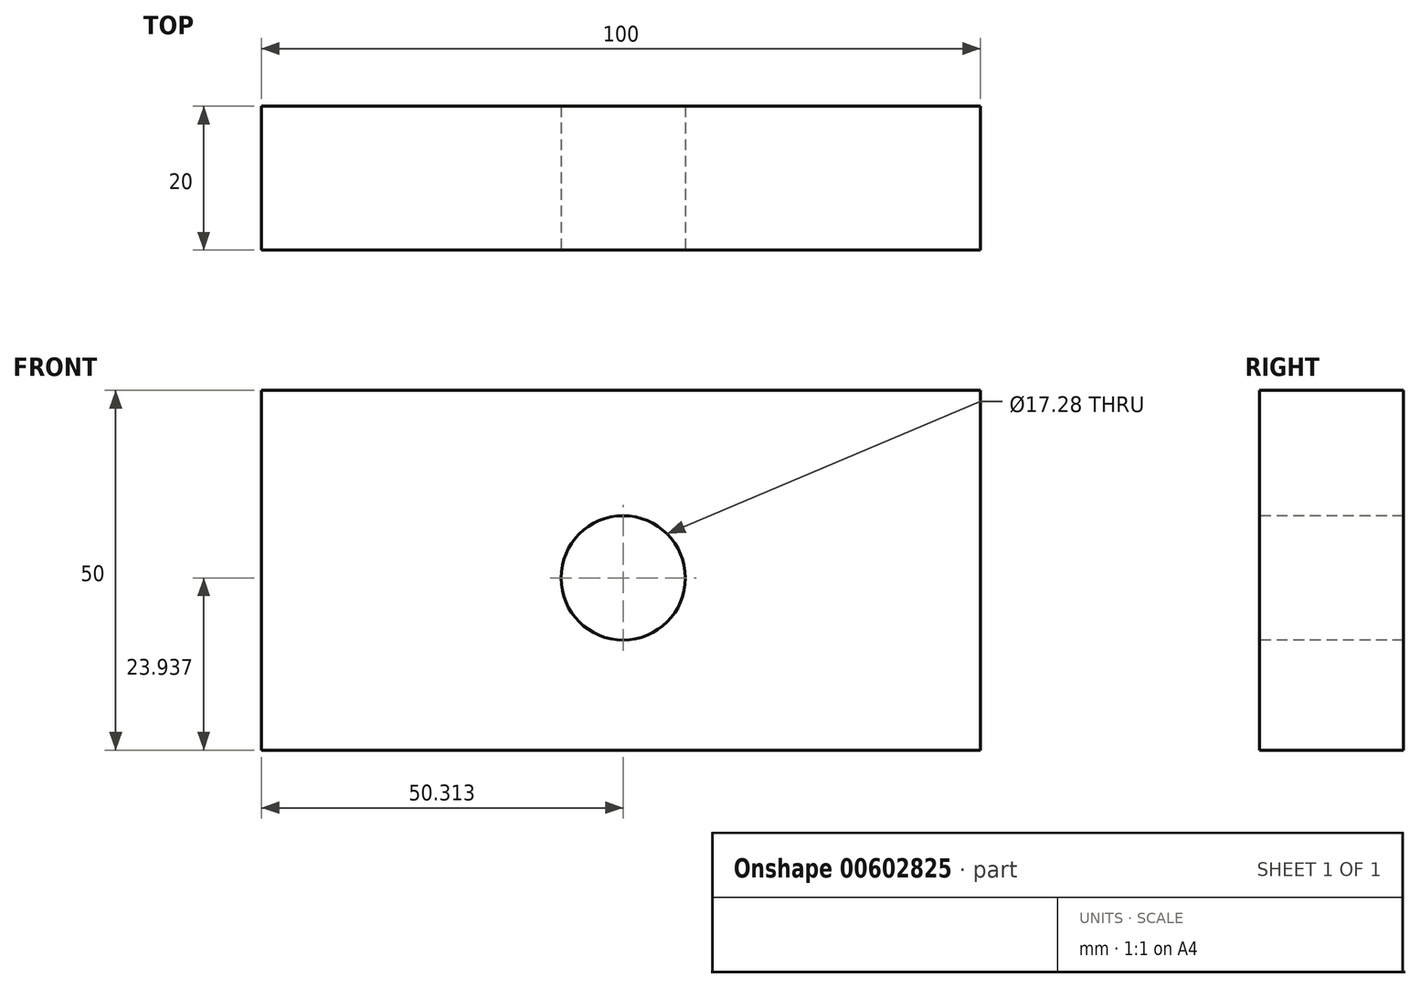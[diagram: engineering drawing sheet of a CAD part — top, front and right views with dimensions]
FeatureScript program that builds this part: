
annotation { "Feature Type Name" : "Feature", "Feature Type Description" : "" }
export const myFeature = defineFeature(function(context is Context, id is Id, definition is map)
    precondition{}
    {
        {
            var Q0;
            Q0=qCreatedBy(makeId("Front.planeOp"),FACE);
            var sketch = newSketch(context, id + "F0", { "sketchPlane" : qUnion([Q0])});
            skLineSegment(sketch, "E0.bottom", {"start": v(0, 0) * mm, "end": v(100, 0) * mm});
            skLineSegment(sketch, "E0.top", {"start": v(0, 50) * mm, "end": v(100, 50) * mm});
            skLineSegment(sketch, "E0.left", {"start": v(0, 0) * mm, "end": v(0, 50) * mm});
            skLineSegment(sketch, "E0.right", {"start": v(100, 0) * mm, "end": v(100, 50) * mm});
            skSolve(sketch);
        }
        {
            var Q0;
            Q0=makeQuery(id+"F0.imprint","IMPRINT",FACE,{"disambiguationData":[TD([[makeQuery(id+"F0.imprint","IMPRINT",EDGE,{"derivedFrom":sQuery(id+"F0.wireOp",EDGE,"E0.bottom")}),1.0]])]});
            extrude(context, id + "F1", {"entities" : qUnion([Q0]), "depth" : 20 * mm, "offsetDistance" : 25 * mm});
        }
        {
            var Q0;
            Q0=makeQuery(id+"F1.opExtrude","CAP_FACE",FACE,{"disambiguationData":[OSD([sQuery(id+"F0.wireOp",EDGE,"E0.bottom"),sQuery(id+"F0.wireOp",EDGE,"E0.top"),sQuery(id+"F0.wireOp",EDGE,"E0.left"),sQuery(id+"F0.wireOp",EDGE,"E0.right")])],"isStart":false});
            var sketch = newSketch(context, id + "F2", { "sketchPlane" : qUnion([Q0])});
            skCircle(sketch, "E1", {"center": v(50.31, 23.94) * mm, "radius": 8.64 * mm});
            skSolve(sketch);
        }
        {
            var Q0;
            Q0=makeQuery(id+"F2.imprint","IMPRINT",FACE,{"disambiguationData":[TD([[makeQuery(id+"F2.imprint","IMPRINT",EDGE,{"derivedFrom":sQuery(id+"F2.wireOp",EDGE,"E1")}),1.0]])]});
            var Q1;
            Q1=sQuery(id+"F2.wireOp",EDGE,"E1");
            extrude(context, id + "F3", {"entities" : qUnion([Q0]), "operationType" : NewBodyOperationType.REMOVE, "surfaceEntities" : qUnion([Q1]), "oppositeDirection" : true, "depth" : 20 * mm, "offsetDistance" : 25 * mm});
        }
    });
